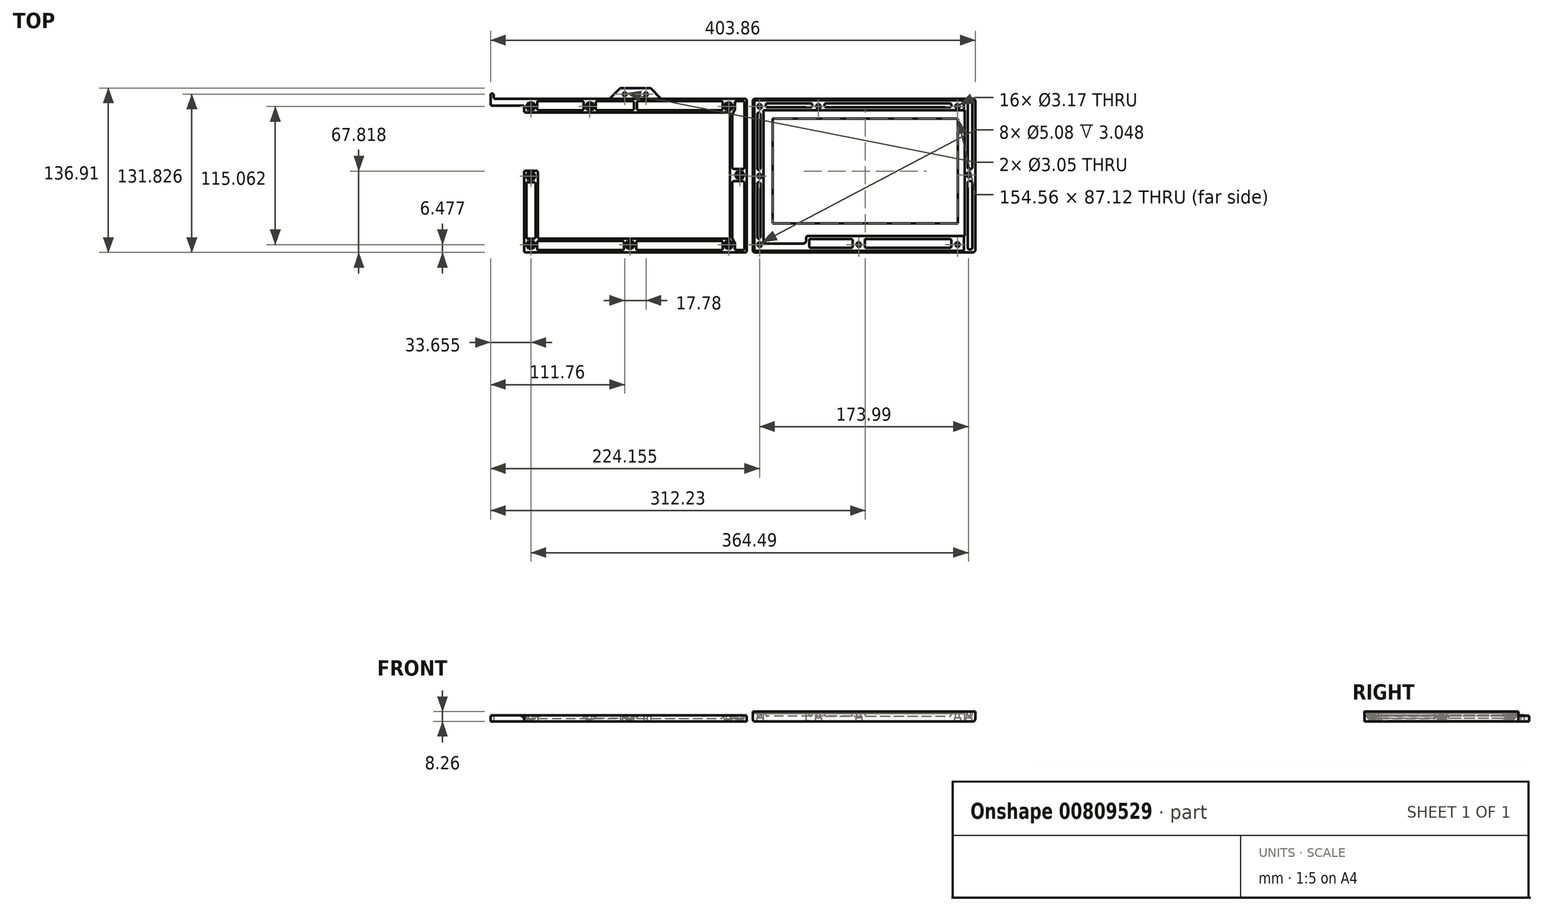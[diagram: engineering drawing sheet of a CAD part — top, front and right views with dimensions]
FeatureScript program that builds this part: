
annotation { "Feature Type Name" : "Feature", "Feature Type Description" : "" }
export const myFeature = defineFeature(function(context is Context, id is Id, definition is map)
    precondition{}
    {
        {
            var Q0;
            Q0=qCreatedBy(makeId("Top.planeOp"),FACE);
            var sketch = newSketch(context, id + "F0", { "sketchPlane" : qUnion([Q0])});
            skLineSegment(sketch, "E0.bottom", {"start": v(2.54, 2.54) * mm, "end": v(187.96, 2.54) * mm});
            skLineSegment(sketch, "E0.top", {"start": v(2.54, 130.56) * mm, "end": v(187.96, 130.56) * mm});
            skLineSegment(sketch, "E0.left", {"start": v(2.54, 2.54) * mm, "end": v(2.54, 130.56) * mm});
            skLineSegment(sketch, "E0.right", {"start": v(187.96, 2.54) * mm, "end": v(187.96, 130.56) * mm});
            skSolve(sketch);
        }
        {
            var Q0;
            Q0 = qSketchRegion(id + "F0", true);
            extrude(context, id + "F1", {"entities" : qUnion([Q0]), "depth" : 8.25 * mm, "offsetDistance" : 25.4 * mm});
        }
        {
            var Q0;
            Q0=makeQuery(id+"F1.opExtrude","CAP_FACE",FACE,{"disambiguationData":[OSD([sQuery(id+"F0.wireOp",EDGE,"E0.bottom"),sQuery(id+"F0.wireOp",EDGE,"E0.top"),sQuery(id+"F0.wireOp",EDGE,"E0.left"),sQuery(id+"F0.wireOp",EDGE,"E0.right")])],"isStart":false});
            var sketch = newSketch(context, id + "F2", { "sketchPlane" : qUnion([Q0])});
            skLineSegment(sketch, "E1.bottom", {"start": v(3.8, 129.29) * mm, "end": v(178.44, 129.29) * mm});
            skLineSegment(sketch, "E1.top", {"start": v(3.81, 3.81) * mm, "end": v(178.44, 3.81) * mm});
            skLineSegment(sketch, "E1.left", {"start": v(3.8, 129.29) * mm, "end": v(3.81, 3.81) * mm});
            skLineSegment(sketch, "E1.right", {"start": v(178.44, 129.29) * mm, "end": v(178.44, 3.81) * mm});
            skSolve(sketch);
        }
        {
            var Q0;
            Q0 = qSketchRegion(id + "F2", true);
            extrude(context, id + "F3", {"entities" : qUnion([Q0]), "operationType" : NewBodyOperationType.REMOVE, "oppositeDirection" : true, "depth" : 1.57 * mm, "offsetDistance" : 25.4 * mm});
        }
        {
            var Q0;
            Q0=makeQuery(id+"F1.opExtrude","CAP_FACE",FACE,{"disambiguationData":[OSD([sQuery(id+"F0.wireOp",EDGE,"E0.bottom"),sQuery(id+"F0.wireOp",EDGE,"E0.top"),sQuery(id+"F0.wireOp",EDGE,"E0.left"),sQuery(id+"F0.wireOp",EDGE,"E0.right")])],"isStart":false});
            var sketch = newSketch(context, id + "F4", { "sketchPlane" : qUnion([Q0])});
            skLineSegment(sketch, "E2.bottom", {"start": v(11.43, 121.03) * mm, "end": v(179.07, 121.03) * mm});
            skLineSegment(sketch, "E2.top", {"start": v(47, 16.38) * mm, "end": v(179.07, 16.38) * mm});
            skLineSegment(sketch, "E2.left", {"start": v(11.43, 121.03) * mm, "end": v(11.43, 10.03) * mm});
            skLineSegment(sketch, "E2.right", {"start": v(179.07, 121.03) * mm, "end": v(179.07, 16.38) * mm});
            skLineSegment(sketch, "E3.top", {"start": v(11.43, 10.03) * mm, "end": v(47, 10.03) * mm});
            skLineSegment(sketch, "E3.right", {"start": v(47, 16.38) * mm, "end": v(47, 10.03) * mm});
            skSolve(sketch);
        }
        {
            var Q0;
            Q0 = qSketchRegion(id + "F4", true);
            extrude(context, id + "F5", {"entities" : qUnion([Q0]), "operationType" : NewBodyOperationType.REMOVE, "oppositeDirection" : true, "depth" : 7.62 * mm, "offsetDistance" : 25.4 * mm});
        }
        {
            var Q0;
            Q0=makeQuery(id+"F5.boolean.opBoolean","COPY",FACE,{"derivedFrom":makeQuery(id+"F5.opExtrude","CAP_FACE",FACE,{"disambiguationData":[OSD([sQuery(id+"F4.wireOp",EDGE,"E2.bottom"),sQuery(id+"F4.wireOp",EDGE,"E2.top"),sQuery(id+"F4.wireOp",EDGE,"E2.left"),sQuery(id+"F4.wireOp",EDGE,"E2.right")])],"isStart":false})});
            var sketch = newSketch(context, id + "F6", { "sketchPlane" : qUnion([Q0])});
            skLineSegment(sketch, "E4.bottom", {"start": v(19.05, 113.92) * mm, "end": v(173.6, 113.92) * mm});
            skLineSegment(sketch, "E4.top", {"start": v(19.05, 26.8) * mm, "end": v(173.6, 26.8) * mm});
            skLineSegment(sketch, "E4.left", {"start": v(19.05, 113.92) * mm, "end": v(19.05, 26.8) * mm});
            skLineSegment(sketch, "E4.right", {"start": v(173.6, 113.92) * mm, "end": v(173.6, 26.8) * mm});
            skSolve(sketch);
        }
        {
            var Q0;
            Q0 = qSketchRegion(id + "F6", true);
            extrude(context, id + "F7", {"entities" : qUnion([Q0]), "operationType" : NewBodyOperationType.REMOVE, "endBound" : BoundingType.UP_TO_NEXT, "oppositeDirection" : true, "depth" : 25.4 * mm, "offsetDistance" : 25.4 * mm});
        }
        {
            var Q0;
            Q0=makeQuery(id+"F1.opExtrude","CAP_FACE",FACE,{"disambiguationData":[OSD([sQuery(id+"F0.wireOp",EDGE,"E0.bottom"),sQuery(id+"F0.wireOp",EDGE,"E0.top"),sQuery(id+"F0.wireOp",EDGE,"E0.left"),sQuery(id+"F0.wireOp",EDGE,"E0.right")])],"isStart":false});
            var sketch = newSketch(context, id + "F8", { "sketchPlane" : qUnion([Q0])});
            skCircle(sketch, "E5", {"center": v(8.25, 124.08) * mm, "radius": 1.59 * mm});
            skCircle(sketch, "E6", {"center": v(57.28, 124.08) * mm, "radius": 1.59 * mm});
            skCircle(sketch, "E7", {"center": v(173.1, 124.08) * mm, "radius": 1.59 * mm});
            skCircle(sketch, "E8", {"center": v(173.1, 9.02) * mm, "radius": 1.59 * mm});
            skCircle(sketch, "E9", {"center": v(8.25, 9.02) * mm, "radius": 1.59 * mm});
            skCircle(sketch, "E10", {"center": v(8.25, 66.17) * mm, "radius": 1.59 * mm});
            skCircle(sketch, "E11", {"center": v(90.8, 9.02) * mm, "radius": 1.59 * mm});
            skCircle(sketch, "E12", {"center": v(182.25, 67) * mm, "radius": 1.59 * mm});
            skSolve(sketch);
        }
        {
            var Q0;
            Q0 = qSketchRegion(id + "F8", true);
            extrude(context, id + "F9", {"entities" : qUnion([Q0]), "operationType" : NewBodyOperationType.REMOVE, "endBound" : BoundingType.THROUGH_ALL, "oppositeDirection" : true, "depth" : 25.4 * mm, "offsetDistance" : 25.4 * mm});
        }
        {
            var Q0;
            Q0=makeQuery(id+"F1.opExtrude","CAP_FACE",FACE,{"disambiguationData":[OSD([sQuery(id+"F0.wireOp",EDGE,"E0.bottom"),sQuery(id+"F0.wireOp",EDGE,"E0.top"),sQuery(id+"F0.wireOp",EDGE,"E0.left"),sQuery(id+"F0.wireOp",EDGE,"E0.right")])],"isStart":true});
            var sketch = newSketch(context, id + "F10", { "sketchPlane" : qUnion([Q0])});
            skCircle(sketch, "E13", {"center": v(173.1, -124.08) * mm, "radius": 2.54 * mm});
            skCircle(sketch, "E14", {"center": v(182.25, -67) * mm, "radius": 2.54 * mm});
            skCircle(sketch, "E15", {"center": v(173.1, -9.02) * mm, "radius": 2.54 * mm});
            skCircle(sketch, "E16", {"center": v(90.8, -9.02) * mm, "radius": 2.54 * mm});
            skCircle(sketch, "E17", {"center": v(8.25, -9.02) * mm, "radius": 2.54 * mm});
            skCircle(sketch, "E18", {"center": v(8.25, -66.17) * mm, "radius": 2.54 * mm});
            skCircle(sketch, "E19", {"center": v(8.25, -124.08) * mm, "radius": 2.54 * mm});
            skCircle(sketch, "E20", {"center": v(57.28, -124.08) * mm, "radius": 2.54 * mm});
            skSolve(sketch);
        }
        {
            var Q0;
            Q0 = qSketchRegion(id + "F10", true);
            extrude(context, id + "F11", {"entities" : qUnion([Q0]), "operationType" : NewBodyOperationType.REMOVE, "oppositeDirection" : true, "depth" : 3.05 * mm, "offsetDistance" : 25.4 * mm});
        }
        {
            var Q0;
            Q0=makeQuery(id+"F1.opExtrude","CAP_EDGE",EDGE,{"disambiguationData":[OSD([sQuery(id+"F0.wireOp",EDGE,"E0.right")])],"isStart":true});
            var Q1;
            Q1=makeQuery(id+"F1.opExtrude","CAP_EDGE",EDGE,{"disambiguationData":[OSD([sQuery(id+"F0.wireOp",EDGE,"E0.bottom")])],"isStart":true});
            var Q2;
            Q2=makeQuery(id+"F1.opExtrude","CAP_EDGE",EDGE,{"disambiguationData":[OSD([sQuery(id+"F0.wireOp",EDGE,"E0.top")])],"isStart":true});
            var Q3;
            Q3=makeQuery(id+"F1.opExtrude","CAP_EDGE",EDGE,{"disambiguationData":[OSD([sQuery(id+"F0.wireOp",EDGE,"E0.left")])],"isStart":true});
            var Q4;
            Q4=makeQuery(id+"F1.opExtrude","SWEPT_EDGE",EDGE,{"disambiguationData":[OSD([sQuery(id+"F0.wireOp",EDGE,"E0.bottom"),sQuery(id+"F0.wireOp",EDGE,"E0.left")])]});
            var Q5;
            Q5=makeQuery(id+"F1.opExtrude","SWEPT_EDGE",EDGE,{"disambiguationData":[OSD([sQuery(id+"F0.wireOp",EDGE,"E0.top"),sQuery(id+"F0.wireOp",EDGE,"E0.left")])]});
            var Q6;
            Q6=makeQuery(id+"F1.opExtrude","SWEPT_EDGE",EDGE,{"disambiguationData":[OSD([sQuery(id+"F0.wireOp",EDGE,"E0.bottom"),sQuery(id+"F0.wireOp",EDGE,"E0.right")])]});
            var Q7;
            Q7=makeQuery(id+"F1.opExtrude","SWEPT_EDGE",EDGE,{"disambiguationData":[OSD([sQuery(id+"F0.wireOp",EDGE,"E0.top"),sQuery(id+"F0.wireOp",EDGE,"E0.right")])]});
            var Q8;
            Q8=makeQuery(id+"F5.boolean.opBoolean","COPY",EDGE,{"derivedFrom":makeQuery(id+"F5.opExtrude","SWEPT_EDGE",EDGE,{"disambiguationData":[OSD([sQuery(id+"F4.wireOp",EDGE,"E2.left"),sQuery(id+"F4.wireOp",EDGE,"E3.top")])]})});
            var Q9;
            Q9=makeQuery(id+"F5.boolean.opBoolean","COPY",EDGE,{"derivedFrom":makeQuery(id+"F5.opExtrude","SWEPT_EDGE",EDGE,{"disambiguationData":[OSD([sQuery(id+"F4.wireOp",EDGE,"E3.top"),sQuery(id+"F4.wireOp",EDGE,"E3.right")])]})});
            var Q10;
            Q10=makeQuery(id+"F5.boolean.opBoolean","COPY",EDGE,{"derivedFrom":makeQuery(id+"F5.opExtrude","SWEPT_EDGE",EDGE,{"disambiguationData":[OSD([sQuery(id+"F4.wireOp",EDGE,"E2.top"),sQuery(id+"F4.wireOp",EDGE,"E3.right")])]})});
            fillet(context, id + "F12", {"entities" : qUnion([Q0, Q1, Q2, Q3, Q4, Q5, Q6, Q7, Q8, Q9, Q10]), "radius" : 1.9 * mm, "tangentPropagation" : true, "allowEdgeOverflow" : false});
        }
        {
            var Q0;
            Q0=makeQuery(id+"F3.boolean.opBoolean","COPY",EDGE,{"derivedFrom":makeQuery(id+"F3.opExtrude","SWEPT_EDGE",EDGE,{"disambiguationData":[OSD([sQuery(id+"F2.wireOp",EDGE,"E1.bottom"),sQuery(id+"F2.wireOp",EDGE,"E1.left")])]})});
            var Q1;
            Q1=makeQuery(id+"F3.boolean.opBoolean","COPY",EDGE,{"derivedFrom":makeQuery(id+"F3.opExtrude","SWEPT_EDGE",EDGE,{"disambiguationData":[OSD([sQuery(id+"F2.wireOp",EDGE,"E1.top"),sQuery(id+"F2.wireOp",EDGE,"E1.left")])]})});
            var Q2;
            Q2=makeQuery(id+"F3.boolean.opBoolean","COPY",EDGE,{"derivedFrom":makeQuery(id+"F3.opExtrude","SWEPT_EDGE",EDGE,{"disambiguationData":[OSD([sQuery(id+"F2.wireOp",EDGE,"E1.top"),sQuery(id+"F2.wireOp",EDGE,"E1.right")])]})});
            var Q3;
            Q3=makeQuery(id+"F3.boolean.opBoolean","COPY",EDGE,{"derivedFrom":makeQuery(id+"F3.opExtrude","SWEPT_EDGE",EDGE,{"disambiguationData":[OSD([sQuery(id+"F2.wireOp",EDGE,"E1.bottom"),sQuery(id+"F2.wireOp",EDGE,"E1.right")])]})});
            fillet(context, id + "F13", {"entities" : qUnion([Q0, Q1, Q2, Q3]), "radius" : 1.27 * mm, "tangentPropagation" : true, "allowEdgeOverflow" : false});
        }
        {
            var Q0;
            Q0=makeQuery(id+"F1.opExtrude","CAP_FACE",FACE,{"disambiguationData":[OSD([sQuery(id+"F0.wireOp",EDGE,"E0.bottom"),sQuery(id+"F0.wireOp",EDGE,"E0.top"),sQuery(id+"F0.wireOp",EDGE,"E0.left"),sQuery(id+"F0.wireOp",EDGE,"E0.right")])],"isStart":false});
            var sketch = newSketch(context, id + "F14", { "sketchPlane" : qUnion([Q0])});
            skLineSegment(sketch, "E21.bottom", {"start": v(181.6, 128.02) * mm, "end": v(185.42, 128.02) * mm});
            skLineSegment(sketch, "E21.top", {"start": v(181.6, 72.09) * mm, "end": v(185.42, 72.09) * mm});
            skLineSegment(sketch, "E21.left", {"start": v(181.6, 128.02) * mm, "end": v(181.6, 72.09) * mm});
            skLineSegment(sketch, "E21.right", {"start": v(185.42, 128.02) * mm, "end": v(185.42, 72.09) * mm});
            skLineSegment(sketch, "E22.bottom", {"start": v(181.6, 61.93) * mm, "end": v(185.42, 61.93) * mm});
            skLineSegment(sketch, "E22.top", {"start": v(181.6, 5.08) * mm, "end": v(185.42, 5.08) * mm});
            skLineSegment(sketch, "E22.left", {"start": v(181.6, 61.93) * mm, "end": v(181.6, 5.08) * mm});
            skLineSegment(sketch, "E22.right", {"start": v(185.42, 61.93) * mm, "end": v(185.42, 5.08) * mm});
            skLineSegment(sketch, "E23.bottom", {"start": v(95.88, 13.84) * mm, "end": v(168.02, 13.84) * mm});
            skLineSegment(sketch, "E23.top", {"start": v(95.88, 6.35) * mm, "end": v(168.02, 6.35) * mm});
            skLineSegment(sketch, "E23.left", {"start": v(95.88, 13.84) * mm, "end": v(95.88, 6.35) * mm});
            skLineSegment(sketch, "E23.right", {"start": v(168.02, 13.84) * mm, "end": v(168.02, 6.35) * mm});
            skLineSegment(sketch, "E24.bottom", {"start": v(85.72, 13.84) * mm, "end": v(49.53, 13.84) * mm});
            skLineSegment(sketch, "E24.top", {"start": v(85.72, 6.35) * mm, "end": v(49.53, 6.35) * mm});
            skLineSegment(sketch, "E24.left", {"start": v(85.72, 13.84) * mm, "end": v(85.72, 6.35) * mm});
            skLineSegment(sketch, "E24.right", {"start": v(49.53, 13.84) * mm, "end": v(49.53, 6.35) * mm});
            skLineSegment(sketch, "E25.bottom", {"start": v(62.36, 126.75) * mm, "end": v(168.02, 126.75) * mm});
            skLineSegment(sketch, "E25.top", {"start": v(62.36, 123.57) * mm, "end": v(168.02, 123.57) * mm});
            skLineSegment(sketch, "E25.left", {"start": v(62.36, 126.75) * mm, "end": v(62.36, 123.57) * mm});
            skLineSegment(sketch, "E25.right", {"start": v(168.02, 126.75) * mm, "end": v(168.02, 123.57) * mm});
            skLineSegment(sketch, "E26.bottom", {"start": v(52.2, 126.75) * mm, "end": v(13.33, 126.75) * mm});
            skLineSegment(sketch, "E26.top", {"start": v(52.2, 123.57) * mm, "end": v(13.33, 123.57) * mm});
            skLineSegment(sketch, "E26.left", {"start": v(52.2, 126.75) * mm, "end": v(52.2, 123.57) * mm});
            skLineSegment(sketch, "E26.right", {"start": v(13.33, 126.75) * mm, "end": v(13.33, 123.57) * mm});
            skLineSegment(sketch, "E27.bottom", {"start": v(8.89, 119) * mm, "end": v(6.35, 119) * mm});
            skLineSegment(sketch, "E27.top", {"start": v(8.89, 71.25) * mm, "end": v(6.35, 71.25) * mm});
            skLineSegment(sketch, "E27.left", {"start": v(8.89, 119) * mm, "end": v(8.89, 71.25) * mm});
            skLineSegment(sketch, "E27.right", {"start": v(6.35, 119) * mm, "end": v(6.35, 71.25) * mm});
            skLineSegment(sketch, "E28.bottom", {"start": v(8.89, 61.09) * mm, "end": v(6.35, 61.09) * mm});
            skLineSegment(sketch, "E28.top", {"start": v(8.9, 14.1) * mm, "end": v(6.35, 14.1) * mm});
            skLineSegment(sketch, "E28.left", {"start": v(8.89, 61.09) * mm, "end": v(8.9, 14.1) * mm});
            skLineSegment(sketch, "E28.right", {"start": v(6.35, 61.09) * mm, "end": v(6.35, 14.1) * mm});
            skSolve(sketch);
        }
        {
            var Q0;
            Q0 = qSketchRegion(id + "F14", true);
            extrude(context, id + "F15", {"entities" : qUnion([Q0]), "operationType" : NewBodyOperationType.REMOVE, "oppositeDirection" : true, "depth" : 3.8 * mm, "offsetDistance" : 25.4 * mm});
        }
        {
            var Q0;
            Q0=makeQuery(id+"F15.boolean.opBoolean","COPY",EDGE,{"derivedFrom":makeQuery(id+"F15.opExtrude","SWEPT_EDGE",EDGE,{"disambiguationData":[OSD([sQuery(id+"F14.wireOp",EDGE,"E22.bottom"),sQuery(id+"F14.wireOp",EDGE,"E22.right")])]})});
            var Q1;
            Q1=makeQuery(id+"F15.boolean.opBoolean","COPY",EDGE,{"derivedFrom":makeQuery(id+"F15.opExtrude","SWEPT_EDGE",EDGE,{"disambiguationData":[OSD([sQuery(id+"F14.wireOp",EDGE,"E22.bottom"),sQuery(id+"F14.wireOp",EDGE,"E22.left")])]})});
            var Q2;
            Q2=makeQuery(id+"F15.boolean.opBoolean","COPY",EDGE,{"derivedFrom":makeQuery(id+"F15.opExtrude","CAP_EDGE",EDGE,{"disambiguationData":[OSD([sQuery(id+"F14.wireOp",EDGE,"E22.left")])],"isStart":false})});
            var Q3;
            Q3=makeQuery(id+"F15.boolean.opBoolean","COPY",EDGE,{"derivedFrom":makeQuery(id+"F15.opExtrude","CAP_EDGE",EDGE,{"disambiguationData":[OSD([sQuery(id+"F14.wireOp",EDGE,"E22.bottom")])],"isStart":false})});
            var Q4;
            Q4=makeQuery(id+"F15.boolean.opBoolean","COPY",EDGE,{"derivedFrom":makeQuery(id+"F15.opExtrude","CAP_EDGE",EDGE,{"disambiguationData":[OSD([sQuery(id+"F14.wireOp",EDGE,"E22.right")])],"isStart":false})});
            var Q5;
            Q5=makeQuery(id+"F15.boolean.opBoolean","COPY",EDGE,{"derivedFrom":makeQuery(id+"F15.opExtrude","SWEPT_EDGE",EDGE,{"disambiguationData":[OSD([sQuery(id+"F14.wireOp",EDGE,"E22.top"),sQuery(id+"F14.wireOp",EDGE,"E22.right")])]})});
            var Q6;
            Q6=makeQuery(id+"F15.boolean.opBoolean","COPY",EDGE,{"derivedFrom":makeQuery(id+"F15.opExtrude","CAP_EDGE",EDGE,{"disambiguationData":[OSD([sQuery(id+"F14.wireOp",EDGE,"E22.top")])],"isStart":false})});
            var Q7;
            Q7=makeQuery(id+"F15.boolean.opBoolean","COPY",EDGE,{"derivedFrom":makeQuery(id+"F15.opExtrude","SWEPT_EDGE",EDGE,{"disambiguationData":[OSD([sQuery(id+"F14.wireOp",EDGE,"E22.top"),sQuery(id+"F14.wireOp",EDGE,"E22.left")])]})});
            var Q8;
            Q8=makeQuery(id+"F15.boolean.opBoolean","COPY",EDGE,{"derivedFrom":makeQuery(id+"F15.opExtrude","SWEPT_EDGE",EDGE,{"disambiguationData":[OSD([sQuery(id+"F14.wireOp",EDGE,"E21.top"),sQuery(id+"F14.wireOp",EDGE,"E21.left")])]})});
            var Q9;
            Q9=makeQuery(id+"F15.boolean.opBoolean","COPY",EDGE,{"derivedFrom":makeQuery(id+"F15.opExtrude","CAP_EDGE",EDGE,{"disambiguationData":[OSD([sQuery(id+"F14.wireOp",EDGE,"E21.left")])],"isStart":false})});
            var Q10;
            Q10=makeQuery(id+"F15.boolean.opBoolean","COPY",EDGE,{"derivedFrom":makeQuery(id+"F15.opExtrude","CAP_EDGE",EDGE,{"disambiguationData":[OSD([sQuery(id+"F14.wireOp",EDGE,"E21.right")])],"isStart":false})});
            var Q11;
            Q11=makeQuery(id+"F15.boolean.opBoolean","COPY",EDGE,{"derivedFrom":makeQuery(id+"F15.opExtrude","SWEPT_EDGE",EDGE,{"disambiguationData":[OSD([sQuery(id+"F14.wireOp",EDGE,"E21.top"),sQuery(id+"F14.wireOp",EDGE,"E21.right")])]})});
            var Q12;
            Q12=makeQuery(id+"F15.boolean.opBoolean","COPY",EDGE,{"derivedFrom":makeQuery(id+"F15.opExtrude","CAP_EDGE",EDGE,{"disambiguationData":[OSD([sQuery(id+"F14.wireOp",EDGE,"E21.top")])],"isStart":false})});
            var Q13;
            Q13=makeQuery(id+"F15.boolean.opBoolean","COPY",EDGE,{"derivedFrom":makeQuery(id+"F15.opExtrude","SWEPT_EDGE",EDGE,{"disambiguationData":[OSD([sQuery(id+"F14.wireOp",EDGE,"E21.bottom"),sQuery(id+"F14.wireOp",EDGE,"E21.right")])]})});
            var Q14;
            Q14=makeQuery(id+"F15.boolean.opBoolean","COPY",EDGE,{"derivedFrom":makeQuery(id+"F15.opExtrude","CAP_EDGE",EDGE,{"disambiguationData":[OSD([sQuery(id+"F14.wireOp",EDGE,"E21.bottom")])],"isStart":false})});
            var Q15;
            Q15=makeQuery(id+"F15.boolean.opBoolean","COPY",EDGE,{"derivedFrom":makeQuery(id+"F15.opExtrude","SWEPT_EDGE",EDGE,{"disambiguationData":[OSD([sQuery(id+"F14.wireOp",EDGE,"E21.bottom"),sQuery(id+"F14.wireOp",EDGE,"E21.left")])]})});
            var Q16;
            Q16=makeQuery(id+"F15.boolean.opBoolean","COPY",EDGE,{"derivedFrom":makeQuery(id+"F15.opExtrude","SWEPT_EDGE",EDGE,{"disambiguationData":[OSD([sQuery(id+"F14.wireOp",EDGE,"E25.bottom"),sQuery(id+"F14.wireOp",EDGE,"E25.right")])]})});
            var Q17;
            Q17=makeQuery(id+"F15.boolean.opBoolean","COPY",EDGE,{"derivedFrom":makeQuery(id+"F15.opExtrude","CAP_EDGE",EDGE,{"disambiguationData":[OSD([sQuery(id+"F14.wireOp",EDGE,"E25.right")])],"isStart":false})});
            var Q18;
            Q18=makeQuery(id+"F15.boolean.opBoolean","COPY",EDGE,{"derivedFrom":makeQuery(id+"F15.opExtrude","CAP_EDGE",EDGE,{"disambiguationData":[OSD([sQuery(id+"F14.wireOp",EDGE,"E25.bottom")])],"isStart":false})});
            var Q19;
            Q19=makeQuery(id+"F15.boolean.opBoolean","COPY",EDGE,{"derivedFrom":makeQuery(id+"F15.opExtrude","SWEPT_EDGE",EDGE,{"disambiguationData":[OSD([sQuery(id+"F14.wireOp",EDGE,"E25.top"),sQuery(id+"F14.wireOp",EDGE,"E25.right")])]})});
            var Q20;
            Q20=makeQuery(id+"F15.boolean.opBoolean","COPY",EDGE,{"derivedFrom":makeQuery(id+"F15.opExtrude","CAP_EDGE",EDGE,{"disambiguationData":[OSD([sQuery(id+"F14.wireOp",EDGE,"E25.left")])],"isStart":false})});
            var Q21;
            Q21=makeQuery(id+"F15.boolean.opBoolean","COPY",EDGE,{"derivedFrom":makeQuery(id+"F15.opExtrude","SWEPT_EDGE",EDGE,{"disambiguationData":[OSD([sQuery(id+"F14.wireOp",EDGE,"E25.bottom"),sQuery(id+"F14.wireOp",EDGE,"E25.left")])]})});
            var Q22;
            Q22=makeQuery(id+"F15.boolean.opBoolean","COPY",EDGE,{"derivedFrom":makeQuery(id+"F15.opExtrude","SWEPT_EDGE",EDGE,{"disambiguationData":[OSD([sQuery(id+"F14.wireOp",EDGE,"E25.top"),sQuery(id+"F14.wireOp",EDGE,"E25.left")])]})});
            var Q23;
            Q23=makeQuery(id+"F15.boolean.opBoolean","COPY",EDGE,{"derivedFrom":makeQuery(id+"F15.opExtrude","SWEPT_EDGE",EDGE,{"disambiguationData":[OSD([sQuery(id+"F14.wireOp",EDGE,"E26.top"),sQuery(id+"F14.wireOp",EDGE,"E26.right")])]})});
            var Q24;
            Q24=makeQuery(id+"F15.boolean.opBoolean","COPY",EDGE,{"derivedFrom":makeQuery(id+"F15.opExtrude","CAP_EDGE",EDGE,{"disambiguationData":[OSD([sQuery(id+"F14.wireOp",EDGE,"E26.right")])],"isStart":false})});
            var Q25;
            Q25=makeQuery(id+"F15.boolean.opBoolean","COPY",EDGE,{"derivedFrom":makeQuery(id+"F15.opExtrude","CAP_EDGE",EDGE,{"disambiguationData":[OSD([sQuery(id+"F14.wireOp",EDGE,"E26.top")])],"isStart":false})});
            var Q26;
            Q26=makeQuery(id+"F15.boolean.opBoolean","COPY",EDGE,{"derivedFrom":makeQuery(id+"F15.opExtrude","SWEPT_EDGE",EDGE,{"disambiguationData":[OSD([sQuery(id+"F14.wireOp",EDGE,"E26.bottom"),sQuery(id+"F14.wireOp",EDGE,"E26.right")])]})});
            var Q27;
            Q27=makeQuery(id+"F15.boolean.opBoolean","COPY",EDGE,{"derivedFrom":makeQuery(id+"F15.opExtrude","CAP_EDGE",EDGE,{"disambiguationData":[OSD([sQuery(id+"F14.wireOp",EDGE,"E26.left")])],"isStart":false})});
            var Q28;
            Q28=makeQuery(id+"F15.boolean.opBoolean","COPY",EDGE,{"derivedFrom":makeQuery(id+"F15.opExtrude","SWEPT_EDGE",EDGE,{"disambiguationData":[OSD([sQuery(id+"F14.wireOp",EDGE,"E26.bottom"),sQuery(id+"F14.wireOp",EDGE,"E26.left")])]})});
            var Q29;
            Q29=makeQuery(id+"F15.boolean.opBoolean","COPY",EDGE,{"derivedFrom":makeQuery(id+"F15.opExtrude","CAP_EDGE",EDGE,{"disambiguationData":[OSD([sQuery(id+"F14.wireOp",EDGE,"E26.bottom")])],"isStart":false})});
            var Q30;
            Q30=makeQuery(id+"F15.boolean.opBoolean","COPY",EDGE,{"derivedFrom":makeQuery(id+"F15.opExtrude","SWEPT_EDGE",EDGE,{"disambiguationData":[OSD([sQuery(id+"F14.wireOp",EDGE,"E26.top"),sQuery(id+"F14.wireOp",EDGE,"E26.left")])]})});
            var Q31;
            Q31=makeQuery(id+"F15.boolean.opBoolean","COPY",EDGE,{"derivedFrom":makeQuery(id+"F15.opExtrude","SWEPT_EDGE",EDGE,{"disambiguationData":[OSD([sQuery(id+"F14.wireOp",EDGE,"E27.bottom"),sQuery(id+"F14.wireOp",EDGE,"E27.right")])]})});
            var Q32;
            Q32=makeQuery(id+"F15.boolean.opBoolean","COPY",EDGE,{"derivedFrom":makeQuery(id+"F15.opExtrude","CAP_EDGE",EDGE,{"disambiguationData":[OSD([sQuery(id+"F14.wireOp",EDGE,"E27.bottom")])],"isStart":false})});
            var Q33;
            Q33=makeQuery(id+"F15.boolean.opBoolean","COPY",EDGE,{"derivedFrom":makeQuery(id+"F15.opExtrude","SWEPT_EDGE",EDGE,{"disambiguationData":[OSD([sQuery(id+"F14.wireOp",EDGE,"E27.bottom"),sQuery(id+"F14.wireOp",EDGE,"E27.left")])]})});
            var Q34;
            Q34=makeQuery(id+"F15.boolean.opBoolean","COPY",EDGE,{"derivedFrom":makeQuery(id+"F15.opExtrude","CAP_EDGE",EDGE,{"disambiguationData":[OSD([sQuery(id+"F14.wireOp",EDGE,"E27.left")])],"isStart":false})});
            var Q35;
            Q35=makeQuery(id+"F15.boolean.opBoolean","COPY",EDGE,{"derivedFrom":makeQuery(id+"F15.opExtrude","SWEPT_EDGE",EDGE,{"disambiguationData":[OSD([sQuery(id+"F14.wireOp",EDGE,"E28.bottom"),sQuery(id+"F14.wireOp",EDGE,"E28.left")])]})});
            var Q36;
            Q36=makeQuery(id+"F15.boolean.opBoolean","COPY",EDGE,{"derivedFrom":makeQuery(id+"F15.opExtrude","CAP_EDGE",EDGE,{"disambiguationData":[OSD([sQuery(id+"F14.wireOp",EDGE,"E28.left")])],"isStart":false})});
            var Q37;
            Q37=makeQuery(id+"F15.boolean.opBoolean","COPY",EDGE,{"derivedFrom":makeQuery(id+"F15.opExtrude","CAP_EDGE",EDGE,{"disambiguationData":[OSD([sQuery(id+"F14.wireOp",EDGE,"E28.bottom")])],"isStart":false})});
            var Q38;
            Q38=makeQuery(id+"F15.boolean.opBoolean","COPY",EDGE,{"derivedFrom":makeQuery(id+"F15.opExtrude","SWEPT_EDGE",EDGE,{"disambiguationData":[OSD([sQuery(id+"F14.wireOp",EDGE,"E28.bottom"),sQuery(id+"F14.wireOp",EDGE,"E28.right")])]})});
            var Q39;
            Q39=makeQuery(id+"F15.boolean.opBoolean","COPY",EDGE,{"derivedFrom":makeQuery(id+"F15.opExtrude","CAP_EDGE",EDGE,{"disambiguationData":[OSD([sQuery(id+"F14.wireOp",EDGE,"E27.right")])],"isStart":false})});
            var Q40;
            Q40=makeQuery(id+"F15.boolean.opBoolean","COPY",EDGE,{"derivedFrom":makeQuery(id+"F15.opExtrude","SWEPT_EDGE",EDGE,{"disambiguationData":[OSD([sQuery(id+"F14.wireOp",EDGE,"E27.top"),sQuery(id+"F14.wireOp",EDGE,"E27.right")])]})});
            var Q41;
            Q41=makeQuery(id+"F15.boolean.opBoolean","COPY",EDGE,{"derivedFrom":makeQuery(id+"F15.opExtrude","CAP_EDGE",EDGE,{"disambiguationData":[OSD([sQuery(id+"F14.wireOp",EDGE,"E27.top")])],"isStart":false})});
            var Q42;
            Q42=makeQuery(id+"F15.boolean.opBoolean","COPY",EDGE,{"derivedFrom":makeQuery(id+"F15.opExtrude","SWEPT_EDGE",EDGE,{"disambiguationData":[OSD([sQuery(id+"F14.wireOp",EDGE,"E27.top"),sQuery(id+"F14.wireOp",EDGE,"E27.left")])]})});
            var Q43;
            Q43=makeQuery(id+"F15.boolean.opBoolean","COPY",EDGE,{"derivedFrom":makeQuery(id+"F15.opExtrude","SWEPT_EDGE",EDGE,{"disambiguationData":[OSD([sQuery(id+"F14.wireOp",EDGE,"E28.top"),sQuery(id+"F14.wireOp",EDGE,"E28.left")])]})});
            var Q44;
            Q44=makeQuery(id+"F15.boolean.opBoolean","COPY",EDGE,{"derivedFrom":makeQuery(id+"F15.opExtrude","CAP_EDGE",EDGE,{"disambiguationData":[OSD([sQuery(id+"F14.wireOp",EDGE,"E28.top")])],"isStart":false})});
            var Q45;
            Q45=makeQuery(id+"F15.boolean.opBoolean","COPY",EDGE,{"derivedFrom":makeQuery(id+"F15.opExtrude","SWEPT_EDGE",EDGE,{"disambiguationData":[OSD([sQuery(id+"F14.wireOp",EDGE,"E28.top"),sQuery(id+"F14.wireOp",EDGE,"E28.right")])]})});
            var Q46;
            Q46=makeQuery(id+"F15.boolean.opBoolean","COPY",EDGE,{"derivedFrom":makeQuery(id+"F15.opExtrude","CAP_EDGE",EDGE,{"disambiguationData":[OSD([sQuery(id+"F14.wireOp",EDGE,"E28.right")])],"isStart":false})});
            var Q47;
            Q47=makeQuery(id+"F15.boolean.opBoolean","COPY",EDGE,{"derivedFrom":makeQuery(id+"F15.opExtrude","SWEPT_EDGE",EDGE,{"disambiguationData":[OSD([sQuery(id+"F14.wireOp",EDGE,"E24.top"),sQuery(id+"F14.wireOp",EDGE,"E24.right")])]})});
            var Q48;
            Q48=makeQuery(id+"F15.boolean.opBoolean","COPY",EDGE,{"derivedFrom":makeQuery(id+"F15.opExtrude","CAP_EDGE",EDGE,{"disambiguationData":[OSD([sQuery(id+"F14.wireOp",EDGE,"E24.right")])],"isStart":false})});
            var Q49;
            Q49=makeQuery(id+"F15.boolean.opBoolean","COPY",EDGE,{"derivedFrom":makeQuery(id+"F15.opExtrude","CAP_EDGE",EDGE,{"disambiguationData":[OSD([sQuery(id+"F14.wireOp",EDGE,"E24.top")])],"isStart":false})});
            var Q50;
            Q50=makeQuery(id+"F15.boolean.opBoolean","COPY",EDGE,{"derivedFrom":makeQuery(id+"F15.opExtrude","SWEPT_EDGE",EDGE,{"disambiguationData":[OSD([sQuery(id+"F14.wireOp",EDGE,"E24.bottom"),sQuery(id+"F14.wireOp",EDGE,"E24.right")])]})});
            var Q51;
            Q51=makeQuery(id+"F15.boolean.opBoolean","COPY",EDGE,{"derivedFrom":makeQuery(id+"F15.opExtrude","CAP_EDGE",EDGE,{"disambiguationData":[OSD([sQuery(id+"F14.wireOp",EDGE,"E24.bottom")])],"isStart":false})});
            var Q52;
            Q52=makeQuery(id+"F15.boolean.opBoolean","COPY",FACE,{"derivedFrom":makeQuery(id+"F15.opExtrude","CAP_FACE",FACE,{"disambiguationData":[OSD([sQuery(id+"F14.wireOp",EDGE,"E23.bottom"),sQuery(id+"F14.wireOp",EDGE,"E23.top"),sQuery(id+"F14.wireOp",EDGE,"E23.left"),sQuery(id+"F14.wireOp",EDGE,"E23.right")])],"isStart":false})});
            var Q53;
            Q53=makeQuery(id+"F15.boolean.opBoolean","COPY",EDGE,{"derivedFrom":makeQuery(id+"F15.opExtrude","SWEPT_EDGE",EDGE,{"disambiguationData":[OSD([sQuery(id+"F14.wireOp",EDGE,"E23.top"),sQuery(id+"F14.wireOp",EDGE,"E23.left")])]})});
            var Q54;
            Q54=makeQuery(id+"F15.boolean.opBoolean","COPY",EDGE,{"derivedFrom":makeQuery(id+"F15.opExtrude","CAP_EDGE",EDGE,{"disambiguationData":[OSD([sQuery(id+"F14.wireOp",EDGE,"E24.left")])],"isStart":false})});
            var Q55;
            Q55=makeQuery(id+"F15.boolean.opBoolean","COPY",EDGE,{"derivedFrom":makeQuery(id+"F15.opExtrude","SWEPT_EDGE",EDGE,{"disambiguationData":[OSD([sQuery(id+"F14.wireOp",EDGE,"E24.top"),sQuery(id+"F14.wireOp",EDGE,"E24.left")])]})});
            var Q56;
            Q56=makeQuery(id+"F15.boolean.opBoolean","COPY",EDGE,{"derivedFrom":makeQuery(id+"F15.opExtrude","SWEPT_EDGE",EDGE,{"disambiguationData":[OSD([sQuery(id+"F14.wireOp",EDGE,"E24.bottom"),sQuery(id+"F14.wireOp",EDGE,"E24.left")])]})});
            var Q57;
            Q57=makeQuery(id+"F15.boolean.opBoolean","COPY",EDGE,{"derivedFrom":makeQuery(id+"F15.opExtrude","SWEPT_EDGE",EDGE,{"disambiguationData":[OSD([sQuery(id+"F14.wireOp",EDGE,"E23.bottom"),sQuery(id+"F14.wireOp",EDGE,"E23.left")])]})});
            var Q58;
            Q58=makeQuery(id+"F15.boolean.opBoolean","COPY",EDGE,{"derivedFrom":makeQuery(id+"F15.opExtrude","SWEPT_EDGE",EDGE,{"disambiguationData":[OSD([sQuery(id+"F14.wireOp",EDGE,"E23.top"),sQuery(id+"F14.wireOp",EDGE,"E23.right")])]})});
            var Q59;
            Q59=makeQuery(id+"F15.boolean.opBoolean","COPY",EDGE,{"derivedFrom":makeQuery(id+"F15.opExtrude","SWEPT_EDGE",EDGE,{"disambiguationData":[OSD([sQuery(id+"F14.wireOp",EDGE,"E23.bottom"),sQuery(id+"F14.wireOp",EDGE,"E23.right")])]})});
            fillet(context, id + "F16", {"entities" : qUnion([Q0, Q1, Q2, Q3, Q4, Q5, Q6, Q7, Q8, Q9, Q10, Q11, Q12, Q13, Q14, Q15, Q16, Q17, Q18, Q19, Q20, Q21, Q22, Q23, Q24, Q25, Q26, Q27, Q28, Q29, Q30, Q31, Q32, Q33, Q34, Q35, Q36, Q37, Q38, Q39, Q40, Q41, Q42, Q43, Q44, Q45, Q46, Q47, Q48, Q49, Q50, Q51, Q52, Q53, Q54, Q55, Q56, Q57, Q58, Q59]), "radius" : 1.27 * mm, "tangentPropagation" : true, "allowEdgeOverflow" : false});
        }
        {
            var Q0;
            Q0=qCreatedBy(makeId("Top.planeOp"),FACE);
            var sketch = newSketch(context, id + "F17", { "sketchPlane" : qUnion([Q0])});
            skLineSegment(sketch, "E29.bottom", {"start": v(-187.96, 2.54) * mm, "end": v(-2.54, 2.54) * mm});
            skLineSegment(sketch, "E29.top", {"start": v(-187.96, 130.56) * mm, "end": v(-2.54, 130.56) * mm});
            skLineSegment(sketch, "E29.left", {"start": v(-187.96, 2.54) * mm, "end": v(-187.96, 70.61) * mm});
            skLineSegment(sketch, "E29.right", {"start": v(-2.54, 2.54) * mm, "end": v(-2.54, 130.56) * mm});
            skLineSegment(sketch, "E30.bottom", {"start": v(-187.96, 119.13) * mm, "end": v(-16.26, 119.13) * mm});
            skLineSegment(sketch, "E30.top", {"start": v(-176.53, 13.97) * mm, "end": v(-16.26, 13.97) * mm});
            skLineSegment(sketch, "E30.left", {"start": v(-176.53, 70.61) * mm, "end": v(-176.53, 13.97) * mm});
            skLineSegment(sketch, "E30.right", {"start": v(-16.26, 119.13) * mm, "end": v(-16.26, 13.97) * mm});
            skLineSegment(sketch, "E31", {"start": v(-176.53, 70.61) * mm, "end": v(-187.96, 70.61) * mm});
            skLineSegment(sketch, "E32.trimOffspring", {"start": v(-187.96, 119.13) * mm, "end": v(-187.96, 124.84) * mm});
            skCircle(sketch, "E33", {"center": v(-182.25, 124.08) * mm, "radius": 1.59 * mm});
            skCircle(sketch, "E34", {"center": v(-133.22, 124.08) * mm, "radius": 1.59 * mm});
            skCircle(sketch, "E35", {"center": v(-17.4, 124.08) * mm, "radius": 1.59 * mm});
            skCircle(sketch, "E36", {"center": v(-17.4, 9.02) * mm, "radius": 1.59 * mm});
            skCircle(sketch, "E37", {"center": v(-182.25, 9.02) * mm, "radius": 1.59 * mm});
            skCircle(sketch, "E38", {"center": v(-182.25, 66.17) * mm, "radius": 1.59 * mm});
            skCircle(sketch, "E39", {"center": v(-99.7, 9.02) * mm, "radius": 1.59 * mm});
            skCircle(sketch, "E40", {"center": v(-8.26, 67) * mm, "radius": 1.59 * mm});
            skLineSegment(sketch, "E41", {"start": v(-116.84, 130.56) * mm, "end": v(-107.95, 139.45) * mm});
            skLineSegment(sketch, "E42", {"start": v(-107.95, 139.45) * mm, "end": v(-82.55, 139.45) * mm});
            skLineSegment(sketch, "E43", {"start": v(-82.55, 139.45) * mm, "end": v(-73.66, 130.56) * mm});
            skLineSegment(sketch, "E44", {"start": v(-187.96, 130.56) * mm, "end": v(-213.36, 130.56) * mm});
            skLineSegment(sketch, "E45", {"start": v(-213.36, 130.56) * mm, "end": v(-213.36, 135) * mm});
            skLineSegment(sketch, "E46", {"start": v(-213.36, 135) * mm, "end": v(-215.9, 135) * mm});
            skLineSegment(sketch, "E47", {"start": v(-215.9, 135) * mm, "end": v(-215.9, 124.84) * mm});
            skLineSegment(sketch, "E48", {"start": v(-215.9, 124.84) * mm, "end": v(-187.96, 124.84) * mm});
            skSolve(sketch);
        }
        {
            var Q0;
            Q0 = qSketchRegion(id + "F17", true);
            extrude(context, id + "F18", {"entities" : qUnion([Q0]), "depth" : 5.08 * mm, "offsetDistance" : 25.4 * mm});
        }
        {
            var Q0;
            Q0=makeQuery(id+"F18.opExtrude","CAP_FACE",FACE,{"disambiguationData":[OSD([sQuery(id+"F17.wireOp",EDGE,"E29.bottom"),sQuery(id+"F17.wireOp",EDGE,"E29.top"),sQuery(id+"F17.wireOp",EDGE,"E29.left"),sQuery(id+"F17.wireOp",EDGE,"E29.right"),sQuery(id+"F17.wireOp",EDGE,"E30.bottom"),sQuery(id+"F17.wireOp",EDGE,"E30.top"),sQuery(id+"F17.wireOp",EDGE,"E30.left"),sQuery(id+"F17.wireOp",EDGE,"E30.right"),sQuery(id+"F17.wireOp",EDGE,"E31"),sQuery(id+"F17.wireOp",EDGE,"E32.trimOffspring"),sQuery(id+"F17.wireOp",EDGE,"E33"),sQuery(id+"F17.wireOp",EDGE,"E34"),sQuery(id+"F17.wireOp",EDGE,"E35"),sQuery(id+"F17.wireOp",EDGE,"E36"),sQuery(id+"F17.wireOp",EDGE,"E37"),sQuery(id+"F17.wireOp",EDGE,"E38"),sQuery(id+"F17.wireOp",EDGE,"E39"),sQuery(id+"F17.wireOp",EDGE,"E40")])],"isStart":false});
            var sketch = newSketch(context, id + "F19", { "sketchPlane" : qUnion([Q0])});
            skCircle(sketch, "E49.cCircle", {"center": v(-182.25, 124.08) * mm, "radius": 3.18 * mm, "construction": true});
            skLineSegment(sketch, "E49.0", {"start": v(-178.58, 124.08) * mm, "end": v(-180.41, 120.9) * mm});
            skLineSegment(sketch, "E49.1", {"start": v(-180.41, 120.9) * mm, "end": v(-184.08, 120.9) * mm});
            skLineSegment(sketch, "E49.2", {"start": v(-184.08, 120.9) * mm, "end": v(-185.91, 124.08) * mm});
            skLineSegment(sketch, "E49.3", {"start": v(-185.91, 124.08) * mm, "end": v(-184.08, 127.25) * mm});
            skLineSegment(sketch, "E49.4", {"start": v(-184.08, 127.25) * mm, "end": v(-180.41, 127.25) * mm});
            skLineSegment(sketch, "E49.5", {"start": v(-180.41, 127.25) * mm, "end": v(-178.58, 124.08) * mm});
            skPoint(sketch, "E49.0.midPoint", {"position": v(-179.5, 122.5) * mm});
            skCircle(sketch, "E50.cCircle", {"center": v(-133.22, 124.08) * mm, "radius": 3.18 * mm, "construction": true});
            skLineSegment(sketch, "E50.0", {"start": v(-129.56, 124.08) * mm, "end": v(-131.39, 120.9) * mm});
            skLineSegment(sketch, "E50.1", {"start": v(-131.39, 120.9) * mm, "end": v(-135.06, 120.9) * mm});
            skLineSegment(sketch, "E50.2", {"start": v(-135.06, 120.9) * mm, "end": v(-136.89, 124.08) * mm});
            skLineSegment(sketch, "E50.3", {"start": v(-136.89, 124.08) * mm, "end": v(-135.06, 127.25) * mm});
            skLineSegment(sketch, "E50.4", {"start": v(-135.06, 127.25) * mm, "end": v(-131.39, 127.25) * mm});
            skLineSegment(sketch, "E50.5", {"start": v(-131.39, 127.25) * mm, "end": v(-129.56, 124.08) * mm});
            skPoint(sketch, "E50.0.midPoint", {"position": v(-130.47, 122.5) * mm});
            skCircle(sketch, "E51.cCircle", {"center": v(-17.4, 124.08) * mm, "radius": 3.18 * mm, "construction": true});
            skLineSegment(sketch, "E51.0", {"start": v(-13.73, 124.08) * mm, "end": v(-15.57, 120.9) * mm});
            skLineSegment(sketch, "E51.1", {"start": v(-15.57, 120.9) * mm, "end": v(-19.23, 120.9) * mm});
            skLineSegment(sketch, "E51.2", {"start": v(-19.23, 120.9) * mm, "end": v(-21.07, 124.08) * mm});
            skLineSegment(sketch, "E51.3", {"start": v(-21.07, 124.08) * mm, "end": v(-19.23, 127.25) * mm});
            skLineSegment(sketch, "E51.4", {"start": v(-19.23, 127.25) * mm, "end": v(-15.57, 127.25) * mm});
            skLineSegment(sketch, "E51.5", {"start": v(-15.57, 127.25) * mm, "end": v(-13.73, 124.08) * mm});
            skPoint(sketch, "E51.0.midPoint", {"position": v(-14.65, 122.5) * mm});
            skCircle(sketch, "E52.cCircle", {"center": v(-8.26, 67) * mm, "radius": 3.18 * mm, "construction": true});
            skLineSegment(sketch, "E52.0", {"start": v(-4.59, 67) * mm, "end": v(-6.42, 63.83) * mm});
            skLineSegment(sketch, "E52.1", {"start": v(-6.42, 63.83) * mm, "end": v(-10.09, 63.83) * mm});
            skLineSegment(sketch, "E52.2", {"start": v(-10.09, 63.83) * mm, "end": v(-11.92, 67) * mm});
            skLineSegment(sketch, "E52.3", {"start": v(-11.92, 67) * mm, "end": v(-10.09, 70.18) * mm});
            skLineSegment(sketch, "E52.4", {"start": v(-10.09, 70.18) * mm, "end": v(-6.42, 70.18) * mm});
            skLineSegment(sketch, "E52.5", {"start": v(-6.42, 70.18) * mm, "end": v(-4.59, 67) * mm});
            skPoint(sketch, "E52.0.midPoint", {"position": v(-5.5, 65.42) * mm});
            skCircle(sketch, "E53.cCircle", {"center": v(-17.4, 9.02) * mm, "radius": 3.18 * mm, "construction": true});
            skLineSegment(sketch, "E53.0", {"start": v(-13.73, 9.02) * mm, "end": v(-15.57, 5.84) * mm});
            skLineSegment(sketch, "E53.1", {"start": v(-15.57, 5.84) * mm, "end": v(-19.23, 5.84) * mm});
            skLineSegment(sketch, "E53.2", {"start": v(-19.23, 5.84) * mm, "end": v(-21.07, 9.02) * mm});
            skLineSegment(sketch, "E53.3", {"start": v(-21.07, 9.02) * mm, "end": v(-19.23, 12.2) * mm});
            skLineSegment(sketch, "E53.4", {"start": v(-19.23, 12.2) * mm, "end": v(-15.57, 12.2) * mm});
            skLineSegment(sketch, "E53.5", {"start": v(-15.57, 12.2) * mm, "end": v(-13.73, 9.02) * mm});
            skPoint(sketch, "E53.0.midPoint", {"position": v(-14.65, 7.43) * mm});
            skCircle(sketch, "E54.cCircle", {"center": v(-99.7, 9.02) * mm, "radius": 3.18 * mm, "construction": true});
            skLineSegment(sketch, "E54.0", {"start": v(-96.03, 9.02) * mm, "end": v(-97.86, 5.84) * mm});
            skLineSegment(sketch, "E54.1", {"start": v(-97.86, 5.84) * mm, "end": v(-101.53, 5.84) * mm});
            skLineSegment(sketch, "E54.2", {"start": v(-101.53, 5.84) * mm, "end": v(-103.36, 9.02) * mm});
            skLineSegment(sketch, "E54.3", {"start": v(-103.36, 9.02) * mm, "end": v(-101.53, 12.2) * mm});
            skLineSegment(sketch, "E54.4", {"start": v(-101.53, 12.2) * mm, "end": v(-97.86, 12.2) * mm});
            skLineSegment(sketch, "E54.5", {"start": v(-97.86, 12.2) * mm, "end": v(-96.03, 9.02) * mm});
            skPoint(sketch, "E54.0.midPoint", {"position": v(-96.95, 7.43) * mm});
            skCircle(sketch, "E55.cCircle", {"center": v(-182.25, 9.02) * mm, "radius": 3.18 * mm, "construction": true});
            skLineSegment(sketch, "E55.0", {"start": v(-178.58, 9.02) * mm, "end": v(-180.41, 5.84) * mm});
            skLineSegment(sketch, "E55.1", {"start": v(-180.41, 5.84) * mm, "end": v(-184.08, 5.84) * mm});
            skLineSegment(sketch, "E55.2", {"start": v(-184.08, 5.84) * mm, "end": v(-185.91, 9.02) * mm});
            skLineSegment(sketch, "E55.3", {"start": v(-185.91, 9.02) * mm, "end": v(-184.08, 12.2) * mm});
            skLineSegment(sketch, "E55.4", {"start": v(-184.08, 12.2) * mm, "end": v(-180.41, 12.2) * mm});
            skLineSegment(sketch, "E55.5", {"start": v(-180.41, 12.2) * mm, "end": v(-178.58, 9.02) * mm});
            skPoint(sketch, "E55.0.midPoint", {"position": v(-179.5, 7.43) * mm});
            skCircle(sketch, "E56.cCircle", {"center": v(-182.25, 66.17) * mm, "radius": 3.18 * mm, "construction": true});
            skLineSegment(sketch, "E56.0", {"start": v(-178.58, 66.17) * mm, "end": v(-180.41, 63) * mm});
            skLineSegment(sketch, "E56.1", {"start": v(-180.41, 63) * mm, "end": v(-184.08, 63) * mm});
            skLineSegment(sketch, "E56.2", {"start": v(-184.08, 63) * mm, "end": v(-185.91, 66.17) * mm});
            skLineSegment(sketch, "E56.3", {"start": v(-185.91, 66.17) * mm, "end": v(-184.08, 69.34) * mm});
            skLineSegment(sketch, "E56.4", {"start": v(-184.08, 69.34) * mm, "end": v(-180.41, 69.34) * mm});
            skLineSegment(sketch, "E56.5", {"start": v(-180.41, 69.34) * mm, "end": v(-178.58, 66.17) * mm});
            skPoint(sketch, "E56.0.midPoint", {"position": v(-179.5, 64.58) * mm});
            skSolve(sketch);
        }
        {
            var Q0;
            Q0 = qSketchRegion(id + "F19", true);
            extrude(context, id + "F20", {"entities" : qUnion([Q0]), "operationType" : NewBodyOperationType.REMOVE, "oppositeDirection" : true, "depth" : 3.3 * mm, "offsetDistance" : 25.4 * mm});
        }
        {
            var Q0;
            Q0=makeQuery(id+"F18.opExtrude","CAP_FACE",FACE,{"disambiguationData":[OSD([sQuery(id+"F17.wireOp",EDGE,"E29.bottom"),sQuery(id+"F17.wireOp",EDGE,"E29.top"),sQuery(id+"F17.wireOp",EDGE,"E29.left"),sQuery(id+"F17.wireOp",EDGE,"E29.right"),sQuery(id+"F17.wireOp",EDGE,"E30.bottom"),sQuery(id+"F17.wireOp",EDGE,"E30.top"),sQuery(id+"F17.wireOp",EDGE,"E30.left"),sQuery(id+"F17.wireOp",EDGE,"E30.right"),sQuery(id+"F17.wireOp",EDGE,"E31"),sQuery(id+"F17.wireOp",EDGE,"E32.trimOffspring"),sQuery(id+"F17.wireOp",EDGE,"E33"),sQuery(id+"F17.wireOp",EDGE,"E34"),sQuery(id+"F17.wireOp",EDGE,"E35"),sQuery(id+"F17.wireOp",EDGE,"E36"),sQuery(id+"F17.wireOp",EDGE,"E37"),sQuery(id+"F17.wireOp",EDGE,"E38"),sQuery(id+"F17.wireOp",EDGE,"E39"),sQuery(id+"F17.wireOp",EDGE,"E40")])],"isStart":false});
            var sketch = newSketch(context, id + "F21", { "sketchPlane" : qUnion([Q0])});
            skLineSegment(sketch, "E57.left", {"start": v(-177.17, 128.65) * mm, "end": v(-177.17, 121.03) * mm});
            skLineSegment(sketch, "E57.right", {"start": v(-138.3, 128.65) * mm, "end": v(-138.3, 121.03) * mm});
            skLineSegment(sketch, "E58.left", {"start": v(-128.14, 128.65) * mm, "end": v(-128.14, 121.03) * mm});
            skLineSegment(sketch, "E58.right", {"start": v(-22.48, 128.65) * mm, "end": v(-22.48, 121.03) * mm});
            skLineSegment(sketch, "E59.right", {"start": v(-12.32, 128.65) * mm, "end": v(-12.32, 121.45) * mm});
            skLineSegment(sketch, "E60.bottom", {"start": v(-4.44, 61.93) * mm, "end": v(-14.35, 61.93) * mm});
            skLineSegment(sketch, "E61.right", {"start": v(-12.32, 10.45) * mm, "end": v(-12.32, 4.45) * mm});
            skLineSegment(sketch, "E62", {"start": v(-177.17, 121.03) * mm, "end": v(-138.3, 121.03) * mm});
            skLineSegment(sketch, "E63", {"start": v(-4.45, 128.65) * mm, "end": v(-12.32, 128.65) * mm});
            skLineSegment(sketch, "E64.trimOffspring", {"start": v(-128.14, 121.03) * mm, "end": v(-96.52, 121.03) * mm});
            skLineSegment(sketch, "E65.trimOffspring", {"start": v(-138.3, 128.65) * mm, "end": v(-177.17, 128.65) * mm});
            skLineSegment(sketch, "E66.trimOffspring", {"start": v(-22.48, 128.65) * mm, "end": v(-93.98, 128.65) * mm});
            skLineSegment(sketch, "E67", {"start": v(-14.35, 13.97) * mm, "end": v(-14.35, 61.93) * mm});
            skPoint(sketch, "E67.endSnap0", {"position": v(-14.65, 10.6) * mm});
            skLineSegment(sketch, "E68", {"start": v(-4.44, 4.45) * mm, "end": v(-12.32, 4.45) * mm});
            skLineSegment(sketch, "E69.trimOffspring", {"start": v(-4.44, 61.93) * mm, "end": v(-4.44, 4.45) * mm});
            skLineSegment(sketch, "E70.top", {"start": v(-4.44, 72.09) * mm, "end": v(-14.35, 72.09) * mm});
            skLineSegment(sketch, "E70.left", {"start": v(-4.45, 128.65) * mm, "end": v(-4.44, 72.09) * mm});
            skLineSegment(sketch, "E70.right", {"start": v(-14.35, 117.93) * mm, "end": v(-14.35, 72.09) * mm});
            skLineSegment(sketch, "E71", {"start": v(-14.35, 117.93) * mm, "end": v(-12.32, 121.45) * mm});
            skLineSegment(sketch, "E72", {"start": v(-12.32, 10.45) * mm, "end": v(-14.35, 13.97) * mm});
            skLineSegment(sketch, "E73.bottom", {"start": v(-94.62, 12.07) * mm, "end": v(-22.48, 12.07) * mm});
            skLineSegment(sketch, "E73.top", {"start": v(-94.62, 4.45) * mm, "end": v(-22.48, 4.45) * mm});
            skLineSegment(sketch, "E73.left", {"start": v(-94.62, 12.07) * mm, "end": v(-94.62, 4.45) * mm});
            skLineSegment(sketch, "E73.right", {"start": v(-22.48, 12.07) * mm, "end": v(-22.48, 4.45) * mm});
            skLineSegment(sketch, "E74.bottom", {"start": v(-177.17, 12.06) * mm, "end": v(-104.78, 12.07) * mm});
            skLineSegment(sketch, "E74.top", {"start": v(-177.17, 4.44) * mm, "end": v(-104.78, 4.45) * mm});
            skLineSegment(sketch, "E74.left", {"start": v(-177.17, 12.06) * mm, "end": v(-177.17, 4.44) * mm});
            skLineSegment(sketch, "E74.right", {"start": v(-104.78, 12.07) * mm, "end": v(-104.78, 4.45) * mm});
            skLineSegment(sketch, "E75.bottom", {"start": v(-186.05, 61.09) * mm, "end": v(-178.44, 61.09) * mm});
            skLineSegment(sketch, "E75.top", {"start": v(-186.05, 14.1) * mm, "end": v(-178.44, 14.1) * mm});
            skLineSegment(sketch, "E75.left", {"start": v(-186.05, 61.09) * mm, "end": v(-186.05, 14.1) * mm});
            skLineSegment(sketch, "E75.right", {"start": v(-178.44, 61.09) * mm, "end": v(-178.44, 14.1) * mm});
            skLineSegment(sketch, "E76", {"start": v(-96.52, 128.65) * mm, "end": v(-96.52, 121.03) * mm});
            skLineSegment(sketch, "E77", {"start": v(-93.98, 121.03) * mm, "end": v(-93.98, 128.65) * mm});
            skLineSegment(sketch, "E78.trimOffspring", {"start": v(-96.52, 128.65) * mm, "end": v(-128.14, 128.65) * mm});
            skLineSegment(sketch, "E79.trimOffspring", {"start": v(-93.98, 121.03) * mm, "end": v(-22.48, 121.03) * mm});
            skSolve(sketch);
        }
        {
            var Q0;
            Q0 = qSketchRegion(id + "F21", true);
            extrude(context, id + "F22", {"entities" : qUnion([Q0]), "operationType" : NewBodyOperationType.REMOVE, "oppositeDirection" : true, "depth" : 2.54 * mm, "offsetDistance" : 25.4 * mm});
        }
        {
            var Q0;
            Q0=makeQuery(id+"F18.opExtrude","CAP_FACE",FACE,{"disambiguationData":[OSD([sQuery(id+"F17.wireOp",EDGE,"E29.bottom"),sQuery(id+"F17.wireOp",EDGE,"E29.top"),sQuery(id+"F17.wireOp",EDGE,"E29.left"),sQuery(id+"F17.wireOp",EDGE,"E29.right"),sQuery(id+"F17.wireOp",EDGE,"E30.bottom"),sQuery(id+"F17.wireOp",EDGE,"E30.top"),sQuery(id+"F17.wireOp",EDGE,"E30.left"),sQuery(id+"F17.wireOp",EDGE,"E30.right"),sQuery(id+"F17.wireOp",EDGE,"E31"),sQuery(id+"F17.wireOp",EDGE,"E32.trimOffspring"),sQuery(id+"F17.wireOp",EDGE,"E33"),sQuery(id+"F17.wireOp",EDGE,"E34"),sQuery(id+"F17.wireOp",EDGE,"E35"),sQuery(id+"F17.wireOp",EDGE,"E36"),sQuery(id+"F17.wireOp",EDGE,"E37"),sQuery(id+"F17.wireOp",EDGE,"E38"),sQuery(id+"F17.wireOp",EDGE,"E39"),sQuery(id+"F17.wireOp",EDGE,"E40"),sQuery(id+"F17.wireOp",EDGE,"E41"),sQuery(id+"F17.wireOp",EDGE,"E42"),sQuery(id+"F17.wireOp",EDGE,"E43")])],"isStart":false});
            var sketch = newSketch(context, id + "F23", { "sketchPlane" : qUnion([Q0])});
            skLineSegment(sketch, "E80", {"start": v(-107.95, 139.45) * mm, "end": v(-116.84, 130.56) * mm});
            skLineSegment(sketch, "E81", {"start": v(-116.84, 130.56) * mm, "end": v(-73.66, 130.56) * mm});
            skLineSegment(sketch, "E82", {"start": v(-73.66, 130.56) * mm, "end": v(-82.55, 139.45) * mm});
            skLineSegment(sketch, "E83", {"start": v(-82.55, 139.45) * mm, "end": v(-107.95, 139.45) * mm});
            skSolve(sketch);
        }
        {
            var Q0;
            Q0 = qSketchRegion(id + "F23", true);
            extrude(context, id + "F24", {"entities" : qUnion([Q0]), "operationType" : NewBodyOperationType.REMOVE, "oppositeDirection" : true, "depth" : 0.38 * mm, "offsetDistance" : 25.4 * mm});
        }
        {
            var Q0;
            Q0=makeQuery(id+"F22.boolean.opBoolean","COPY",EDGE,{"derivedFrom":makeQuery(id+"F22.opExtrude","SWEPT_EDGE",EDGE,{"disambiguationData":[OSD([sQuery(id+"F21.wireOp",EDGE,"E58.right"),sQuery(id+"F21.wireOp",EDGE,"E64.trimOffspring")])]})});
            var Q1;
            Q1=makeQuery(id+"F22.boolean.opBoolean","COPY",EDGE,{"derivedFrom":makeQuery(id+"F22.opExtrude","SWEPT_EDGE",EDGE,{"disambiguationData":[OSD([sQuery(id+"F21.wireOp",EDGE,"E57.right"),sQuery(id+"F21.wireOp",EDGE,"E62")])]})});
            var Q2;
            Q2=makeQuery(id+"F22.boolean.opBoolean","COPY",EDGE,{"derivedFrom":makeQuery(id+"F22.opExtrude","SWEPT_EDGE",EDGE,{"disambiguationData":[OSD([sQuery(id+"F21.wireOp",EDGE,"E57.right"),sQuery(id+"F21.wireOp",EDGE,"E65.trimOffspring")])]})});
            var Q3;
            Q3=makeQuery(id+"F22.boolean.opBoolean","COPY",EDGE,{"derivedFrom":makeQuery(id+"F22.opExtrude","SWEPT_EDGE",EDGE,{"disambiguationData":[OSD([sQuery(id+"F21.wireOp",EDGE,"E58.right"),sQuery(id+"F21.wireOp",EDGE,"E66.trimOffspring")])]})});
            var Q4;
            Q4=makeQuery(id+"F22.boolean.opBoolean","COPY",EDGE,{"derivedFrom":makeQuery(id+"F22.opExtrude","SWEPT_EDGE",EDGE,{"disambiguationData":[OSD([sQuery(id+"F21.wireOp",EDGE,"E58.left"),sQuery(id+"F21.wireOp",EDGE,"E66.trimOffspring")])]})});
            var Q5;
            Q5=makeQuery(id+"F22.boolean.opBoolean","COPY",EDGE,{"derivedFrom":makeQuery(id+"F22.opExtrude","SWEPT_EDGE",EDGE,{"disambiguationData":[OSD([sQuery(id+"F21.wireOp",EDGE,"E57.left"),sQuery(id+"F21.wireOp",EDGE,"E65.trimOffspring")])]})});
            var Q6;
            Q6=makeQuery(id+"F22.boolean.opBoolean","COPY",EDGE,{"derivedFrom":makeQuery(id+"F22.opExtrude","SWEPT_EDGE",EDGE,{"disambiguationData":[OSD([sQuery(id+"F21.wireOp",EDGE,"E58.left"),sQuery(id+"F21.wireOp",EDGE,"E64.trimOffspring")])]})});
            var Q7;
            Q7=makeQuery(id+"F22.boolean.opBoolean","COPY",EDGE,{"derivedFrom":makeQuery(id+"F22.opExtrude","SWEPT_EDGE",EDGE,{"disambiguationData":[OSD([sQuery(id+"F21.wireOp",EDGE,"E57.left"),sQuery(id+"F21.wireOp",EDGE,"E62")])]})});
            var Q8;
            Q8=makeQuery(id+"F22.boolean.opBoolean","COPY",EDGE,{"derivedFrom":makeQuery(id+"F22.opExtrude","SWEPT_EDGE",EDGE,{"disambiguationData":[OSD([sQuery(id+"F21.wireOp",EDGE,"E70.top"),sQuery(id+"F21.wireOp",EDGE,"E70.left")])]})});
            var Q9;
            Q9=makeQuery(id+"F22.boolean.opBoolean","COPY",EDGE,{"derivedFrom":makeQuery(id+"F22.opExtrude","SWEPT_EDGE",EDGE,{"disambiguationData":[OSD([sQuery(id+"F21.wireOp",EDGE,"E68"),sQuery(id+"F21.wireOp",EDGE,"E69.trimOffspring")])]})});
            var Q10;
            Q10=makeQuery(id+"F22.boolean.opBoolean","COPY",EDGE,{"derivedFrom":makeQuery(id+"F22.opExtrude","SWEPT_EDGE",EDGE,{"disambiguationData":[OSD([sQuery(id+"F21.wireOp",EDGE,"E61.right"),sQuery(id+"F21.wireOp",EDGE,"E72")])]})});
            var Q11;
            Q11=makeQuery(id+"F22.boolean.opBoolean","COPY",EDGE,{"derivedFrom":makeQuery(id+"F22.opExtrude","SWEPT_EDGE",EDGE,{"disambiguationData":[OSD([sQuery(id+"F21.wireOp",EDGE,"E70.top"),sQuery(id+"F21.wireOp",EDGE,"E70.right")])]})});
            var Q12;
            Q12=makeQuery(id+"F22.boolean.opBoolean","COPY",EDGE,{"derivedFrom":makeQuery(id+"F22.opExtrude","SWEPT_EDGE",EDGE,{"disambiguationData":[OSD([sQuery(id+"F21.wireOp",EDGE,"E67"),sQuery(id+"F21.wireOp",EDGE,"E72")])]})});
            var Q13;
            Q13=makeQuery(id+"F22.boolean.opBoolean","COPY",EDGE,{"derivedFrom":makeQuery(id+"F22.opExtrude","SWEPT_EDGE",EDGE,{"disambiguationData":[OSD([sQuery(id+"F21.wireOp",EDGE,"E61.right"),sQuery(id+"F21.wireOp",EDGE,"E68")])]})});
            var Q14;
            Q14=makeQuery(id+"F22.boolean.opBoolean","COPY",EDGE,{"derivedFrom":makeQuery(id+"F22.opExtrude","SWEPT_EDGE",EDGE,{"disambiguationData":[OSD([sQuery(id+"F21.wireOp",EDGE,"E60.bottom"),sQuery(id+"F21.wireOp",EDGE,"E69.trimOffspring")])]})});
            var Q15;
            Q15=makeQuery(id+"F22.boolean.opBoolean","COPY",EDGE,{"derivedFrom":makeQuery(id+"F22.opExtrude","SWEPT_EDGE",EDGE,{"disambiguationData":[OSD([sQuery(id+"F21.wireOp",EDGE,"E63"),sQuery(id+"F21.wireOp",EDGE,"E70.left")])]})});
            var Q16;
            Q16=makeQuery(id+"F22.boolean.opBoolean","COPY",EDGE,{"derivedFrom":makeQuery(id+"F22.opExtrude","SWEPT_EDGE",EDGE,{"disambiguationData":[OSD([sQuery(id+"F21.wireOp",EDGE,"E59.right"),sQuery(id+"F21.wireOp",EDGE,"E71")])]})});
            var Q17;
            Q17=makeQuery(id+"F22.boolean.opBoolean","COPY",EDGE,{"derivedFrom":makeQuery(id+"F22.opExtrude","SWEPT_EDGE",EDGE,{"disambiguationData":[OSD([sQuery(id+"F21.wireOp",EDGE,"E70.right"),sQuery(id+"F21.wireOp",EDGE,"E71")])]})});
            var Q18;
            Q18=makeQuery(id+"F22.boolean.opBoolean","COPY",EDGE,{"derivedFrom":makeQuery(id+"F22.opExtrude","SWEPT_EDGE",EDGE,{"disambiguationData":[OSD([sQuery(id+"F21.wireOp",EDGE,"E59.right"),sQuery(id+"F21.wireOp",EDGE,"E63")])]})});
            var Q19;
            Q19=makeQuery(id+"F22.boolean.opBoolean","COPY",EDGE,{"derivedFrom":makeQuery(id+"F22.opExtrude","SWEPT_EDGE",EDGE,{"disambiguationData":[OSD([sQuery(id+"F21.wireOp",EDGE,"E60.bottom"),sQuery(id+"F21.wireOp",EDGE,"E67")])]})});
            var Q20;
            Q20=makeQuery(id+"F22.boolean.opBoolean","COPY",EDGE,{"derivedFrom":makeQuery(id+"F22.opExtrude","SWEPT_EDGE",EDGE,{"disambiguationData":[OSD([sQuery(id+"F21.wireOp",EDGE,"E73.top"),sQuery(id+"F21.wireOp",EDGE,"E73.left")])]})});
            var Q21;
            Q21=makeQuery(id+"F22.boolean.opBoolean","COPY",EDGE,{"derivedFrom":makeQuery(id+"F22.opExtrude","SWEPT_EDGE",EDGE,{"disambiguationData":[OSD([sQuery(id+"F21.wireOp",EDGE,"E74.top"),sQuery(id+"F21.wireOp",EDGE,"E74.left")])]})});
            var Q22;
            Q22=makeQuery(id+"F22.boolean.opBoolean","COPY",EDGE,{"derivedFrom":makeQuery(id+"F22.opExtrude","SWEPT_EDGE",EDGE,{"disambiguationData":[OSD([sQuery(id+"F21.wireOp",EDGE,"E73.bottom"),sQuery(id+"F21.wireOp",EDGE,"E73.left")])]})});
            var Q23;
            Q23=makeQuery(id+"F22.boolean.opBoolean","COPY",EDGE,{"derivedFrom":makeQuery(id+"F22.opExtrude","SWEPT_EDGE",EDGE,{"disambiguationData":[OSD([sQuery(id+"F21.wireOp",EDGE,"E74.bottom"),sQuery(id+"F21.wireOp",EDGE,"E74.left")])]})});
            var Q24;
            Q24=makeQuery(id+"F22.boolean.opBoolean","COPY",EDGE,{"derivedFrom":makeQuery(id+"F22.opExtrude","SWEPT_EDGE",EDGE,{"disambiguationData":[OSD([sQuery(id+"F21.wireOp",EDGE,"E73.bottom"),sQuery(id+"F21.wireOp",EDGE,"E73.right")])]})});
            var Q25;
            Q25=makeQuery(id+"F22.boolean.opBoolean","COPY",EDGE,{"derivedFrom":makeQuery(id+"F22.opExtrude","SWEPT_EDGE",EDGE,{"disambiguationData":[OSD([sQuery(id+"F21.wireOp",EDGE,"E74.bottom"),sQuery(id+"F21.wireOp",EDGE,"E74.right")])]})});
            var Q26;
            Q26=makeQuery(id+"F22.boolean.opBoolean","COPY",EDGE,{"derivedFrom":makeQuery(id+"F22.opExtrude","SWEPT_EDGE",EDGE,{"disambiguationData":[OSD([sQuery(id+"F21.wireOp",EDGE,"E73.top"),sQuery(id+"F21.wireOp",EDGE,"E73.right")])]})});
            var Q27;
            Q27=makeQuery(id+"F22.boolean.opBoolean","COPY",EDGE,{"derivedFrom":makeQuery(id+"F22.opExtrude","SWEPT_EDGE",EDGE,{"disambiguationData":[OSD([sQuery(id+"F21.wireOp",EDGE,"E74.top"),sQuery(id+"F21.wireOp",EDGE,"E74.right")])]})});
            var Q28;
            Q28=makeQuery(id+"F22.boolean.opBoolean","COPY",EDGE,{"derivedFrom":makeQuery(id+"F22.opExtrude","SWEPT_EDGE",EDGE,{"disambiguationData":[OSD([sQuery(id+"F21.wireOp",EDGE,"E75.top"),sQuery(id+"F21.wireOp",EDGE,"E75.right")])]})});
            var Q29;
            Q29=makeQuery(id+"F22.boolean.opBoolean","COPY",EDGE,{"derivedFrom":makeQuery(id+"F22.opExtrude","SWEPT_EDGE",EDGE,{"disambiguationData":[OSD([sQuery(id+"F21.wireOp",EDGE,"E75.top"),sQuery(id+"F21.wireOp",EDGE,"E75.left")])]})});
            var Q30;
            Q30=makeQuery(id+"F22.boolean.opBoolean","COPY",EDGE,{"derivedFrom":makeQuery(id+"F22.opExtrude","SWEPT_EDGE",EDGE,{"disambiguationData":[OSD([sQuery(id+"F21.wireOp",EDGE,"E75.bottom"),sQuery(id+"F21.wireOp",EDGE,"E75.right")])]})});
            var Q31;
            Q31=makeQuery(id+"F22.boolean.opBoolean","COPY",EDGE,{"derivedFrom":makeQuery(id+"F22.opExtrude","SWEPT_EDGE",EDGE,{"disambiguationData":[OSD([sQuery(id+"F21.wireOp",EDGE,"E75.bottom"),sQuery(id+"F21.wireOp",EDGE,"E75.left")])]})});
            var Q32;
            Q32=makeQuery(id+"F22.boolean.opBoolean","COPY",FACE,{"derivedFrom":makeQuery(id+"F22.opExtrude","CAP_FACE",FACE,{"disambiguationData":[OSD([sQuery(id+"F21.wireOp",EDGE,"E75.bottom"),sQuery(id+"F21.wireOp",EDGE,"E75.top"),sQuery(id+"F21.wireOp",EDGE,"E75.left"),sQuery(id+"F21.wireOp",EDGE,"E75.right")])],"isStart":false})});
            var Q33;
            Q33=makeQuery(id+"F22.boolean.opBoolean","COPY",FACE,{"derivedFrom":makeQuery(id+"F22.opExtrude","CAP_FACE",FACE,{"disambiguationData":[OSD([sQuery(id+"F21.wireOp",EDGE,"E74.bottom"),sQuery(id+"F21.wireOp",EDGE,"E74.top"),sQuery(id+"F21.wireOp",EDGE,"E74.left"),sQuery(id+"F21.wireOp",EDGE,"E74.right")])],"isStart":false})});
            var Q34;
            Q34=makeQuery(id+"F22.boolean.opBoolean","COPY",FACE,{"derivedFrom":makeQuery(id+"F22.opExtrude","CAP_FACE",FACE,{"disambiguationData":[OSD([sQuery(id+"F21.wireOp",EDGE,"E73.bottom"),sQuery(id+"F21.wireOp",EDGE,"E73.top"),sQuery(id+"F21.wireOp",EDGE,"E73.left"),sQuery(id+"F21.wireOp",EDGE,"E73.right")])],"isStart":false})});
            var Q35;
            Q35=makeQuery(id+"F22.boolean.opBoolean","COPY",FACE,{"derivedFrom":makeQuery(id+"F22.opExtrude","CAP_FACE",FACE,{"disambiguationData":[OSD([sQuery(id+"F21.wireOp",EDGE,"E60.bottom"),sQuery(id+"F21.wireOp",EDGE,"E61.right"),sQuery(id+"F21.wireOp",EDGE,"E67"),sQuery(id+"F21.wireOp",EDGE,"E68"),sQuery(id+"F21.wireOp",EDGE,"E69.trimOffspring"),sQuery(id+"F21.wireOp",EDGE,"E72")])],"isStart":false})});
            var Q36;
            Q36=makeQuery(id+"F22.boolean.opBoolean","COPY",FACE,{"derivedFrom":makeQuery(id+"F22.opExtrude","CAP_FACE",FACE,{"disambiguationData":[OSD([sQuery(id+"F21.wireOp",EDGE,"E59.right"),sQuery(id+"F21.wireOp",EDGE,"E63"),sQuery(id+"F21.wireOp",EDGE,"E70.top"),sQuery(id+"F21.wireOp",EDGE,"E70.left"),sQuery(id+"F21.wireOp",EDGE,"E70.right"),sQuery(id+"F21.wireOp",EDGE,"E71")])],"isStart":false})});
            var Q37;
            Q37=makeQuery(id+"F22.boolean.opBoolean","COPY",FACE,{"derivedFrom":makeQuery(id+"F22.opExtrude","CAP_FACE",FACE,{"disambiguationData":[OSD([sQuery(id+"F21.wireOp",EDGE,"E58.left"),sQuery(id+"F21.wireOp",EDGE,"E58.right"),sQuery(id+"F21.wireOp",EDGE,"E64.trimOffspring"),sQuery(id+"F21.wireOp",EDGE,"E66.trimOffspring")])],"isStart":false})});
            var Q38;
            Q38=makeQuery(id+"F22.boolean.opBoolean","COPY",FACE,{"derivedFrom":makeQuery(id+"F22.opExtrude","CAP_FACE",FACE,{"disambiguationData":[OSD([sQuery(id+"F21.wireOp",EDGE,"E57.left"),sQuery(id+"F21.wireOp",EDGE,"E57.right"),sQuery(id+"F21.wireOp",EDGE,"E62"),sQuery(id+"F21.wireOp",EDGE,"E65.trimOffspring")])],"isStart":false})});
            var Q39;
            Q39=makeQuery(id+"F18.opExtrude","SWEPT_EDGE",EDGE,{"disambiguationData":[OSD([sQuery(id+"F17.wireOp",EDGE,"E29.bottom"),sQuery(id+"F17.wireOp",EDGE,"E29.left")])]});
            var Q40;
            Q40=makeQuery(id+"F18.opExtrude","SWEPT_EDGE",EDGE,{"disambiguationData":[OSD([sQuery(id+"F17.wireOp",EDGE,"E29.left"),sQuery(id+"F17.wireOp",EDGE,"E31")])]});
            var Q41;
            Q41=makeQuery(id+"F18.opExtrude","SWEPT_EDGE",EDGE,{"disambiguationData":[OSD([sQuery(id+"F17.wireOp",EDGE,"E30.left"),sQuery(id+"F17.wireOp",EDGE,"E31")])]});
            var Q42;
            Q42=makeQuery(id+"F18.opExtrude","SWEPT_EDGE",EDGE,{"disambiguationData":[OSD([sQuery(id+"F17.wireOp",EDGE,"E30.top"),sQuery(id+"F17.wireOp",EDGE,"E30.left")])]});
            var Q43;
            Q43=makeQuery(id+"F18.opExtrude","SWEPT_EDGE",EDGE,{"disambiguationData":[OSD([sQuery(id+"F17.wireOp",EDGE,"E30.top"),sQuery(id+"F17.wireOp",EDGE,"E30.right")])]});
            var Q44;
            Q44=makeQuery(id+"F18.opExtrude","SWEPT_EDGE",EDGE,{"disambiguationData":[OSD([sQuery(id+"F17.wireOp",EDGE,"E30.bottom"),sQuery(id+"F17.wireOp",EDGE,"E30.right")])]});
            var Q45;
            Q45=makeQuery(id+"F18.opExtrude","SWEPT_EDGE",EDGE,{"disambiguationData":[OSD([sQuery(id+"F17.wireOp",EDGE,"E30.bottom"),sQuery(id+"F17.wireOp",EDGE,"E32.trimOffspring")])]});
            var Q46;
            Q46=makeQuery(id+"F18.opExtrude","SWEPT_EDGE",EDGE,{"disambiguationData":[OSD([sQuery(id+"F17.wireOp",EDGE,"E29.top"),sQuery(id+"F17.wireOp",EDGE,"E32.trimOffspring")])]});
            var Q47;
            Q47=makeQuery(id+"F18.opExtrude","SWEPT_EDGE",EDGE,{"disambiguationData":[OSD([sQuery(id+"F17.wireOp",EDGE,"E29.top"),sQuery(id+"F17.wireOp",EDGE,"E29.right")])]});
            var Q48;
            Q48=makeQuery(id+"F22.boolean.opBoolean","COPY",EDGE,{"derivedFrom":makeQuery(id+"F22.opExtrude","SWEPT_EDGE",EDGE,{"disambiguationData":[OSD([sQuery(id+"F21.wireOp",EDGE,"E76"),sQuery(id+"F21.wireOp",EDGE,"E78.trimOffspring")])]})});
            var Q49;
            Q49=makeQuery(id+"F22.boolean.opBoolean","COPY",EDGE,{"derivedFrom":makeQuery(id+"F22.opExtrude","SWEPT_EDGE",EDGE,{"disambiguationData":[OSD([sQuery(id+"F21.wireOp",EDGE,"E77"),sQuery(id+"F21.wireOp",EDGE,"E79.trimOffspring")])]})});
            var Q50;
            Q50=makeQuery(id+"F24.boolean.opBoolean","COPY",EDGE,{"derivedFrom":makeQuery(id+"F24.opExtrude","CAP_EDGE",EDGE,{"disambiguationData":[OSD([sQuery(id+"F23.wireOp",EDGE,"E83")])],"isStart":false})});
            var Q51;
            Q51=makeQuery(id+"F18.opExtrude","CAP_EDGE",EDGE,{"disambiguationData":[OSD([sQuery(id+"F17.wireOp",EDGE,"E29.left")])],"isStart":false});
            var Q52;
            Q52=makeQuery(id+"F18.opExtrude","CAP_EDGE",EDGE,{"disambiguationData":[OSD([sQuery(id+"F17.wireOp",EDGE,"E29.bottom")])],"isStart":false});
            var Q53;
            Q53=makeQuery(id+"F18.opExtrude","CAP_EDGE",EDGE,{"disambiguationData":[OSD([sQuery(id+"F17.wireOp",EDGE,"E31")])],"isStart":false});
            var Q54;
            Q54=makeQuery(id+"F18.opExtrude","CAP_EDGE",EDGE,{"disambiguationData":[OSD([sQuery(id+"F17.wireOp",EDGE,"E30.left")])],"isStart":false});
            var Q55;
            Q55=makeQuery(id+"F18.opExtrude","CAP_EDGE",EDGE,{"disambiguationData":[OSD([sQuery(id+"F17.wireOp",EDGE,"E32.trimOffspring")])],"isStart":false});
            var Q56;
            Q56=makeQuery(id+"F18.opExtrude","CAP_EDGE",EDGE,{"disambiguationData":[OSD([sQuery(id+"F17.wireOp",EDGE,"E29.right")])],"isStart":false});
            var Q57;
            Q57=makeQuery(id+"F18.opExtrude","SWEPT_EDGE",EDGE,{"disambiguationData":[OSD([sQuery(id+"F17.wireOp",EDGE,"E29.bottom"),sQuery(id+"F17.wireOp",EDGE,"E29.right")])]});
            var Q58;
            Q58=makeQuery(id+"F18.opExtrude","CAP_EDGE",EDGE,{"disambiguationData":[OSD([sQuery(id+"F17.wireOp",EDGE,"E47")])],"isStart":false});
            var Q59;
            Q59=makeQuery(id+"F18.opExtrude","SWEPT_EDGE",EDGE,{"disambiguationData":[OSD([sQuery(id+"F17.wireOp",EDGE,"E44"),sQuery(id+"F17.wireOp",EDGE,"E45")])]});
            var Q60;
            Q60=makeQuery(id+"F18.opExtrude","SWEPT_EDGE",EDGE,{"disambiguationData":[OSD([sQuery(id+"F17.wireOp",EDGE,"E45"),sQuery(id+"F17.wireOp",EDGE,"E46")])]});
            var Q61;
            Q61=makeQuery(id+"F18.opExtrude","SWEPT_EDGE",EDGE,{"disambiguationData":[OSD([sQuery(id+"F17.wireOp",EDGE,"E46"),sQuery(id+"F17.wireOp",EDGE,"E47")])]});
            var Q62;
            Q62=makeQuery(id+"F18.opExtrude","SWEPT_EDGE",EDGE,{"disambiguationData":[OSD([sQuery(id+"F17.wireOp",EDGE,"E47"),sQuery(id+"F17.wireOp",EDGE,"E48")])]});
            fillet(context, id + "F25", {"entities" : qUnion([Q0, Q1, Q2, Q3, Q4, Q5, Q6, Q7, Q8, Q9, Q10, Q11, Q12, Q13, Q14, Q15, Q16, Q17, Q18, Q19, Q20, Q21, Q22, Q23, Q24, Q25, Q26, Q27, Q28, Q29, Q30, Q31, Q32, Q33, Q34, Q35, Q36, Q37, Q38, Q39, Q40, Q41, Q42, Q43, Q44, Q45, Q46, Q47, Q48, Q49, Q50, Q51, Q52, Q53, Q54, Q55, Q56, Q57, Q58, Q59, Q60, Q61, Q62]), "radius" : 1.27 * mm, "tangentPropagation" : true, "allowEdgeOverflow" : false});
        }
        {
            var Q0;
            Q0=makeQuery(id+"F18.opExtrude","CAP_FACE",FACE,{"disambiguationData":[OSD([sQuery(id+"F17.wireOp",EDGE,"E29.bottom"),sQuery(id+"F17.wireOp",EDGE,"E29.top"),sQuery(id+"F17.wireOp",EDGE,"E29.left"),sQuery(id+"F17.wireOp",EDGE,"E29.right"),sQuery(id+"F17.wireOp",EDGE,"E30.bottom"),sQuery(id+"F17.wireOp",EDGE,"E30.top"),sQuery(id+"F17.wireOp",EDGE,"E30.left"),sQuery(id+"F17.wireOp",EDGE,"E30.right"),sQuery(id+"F17.wireOp",EDGE,"E31"),sQuery(id+"F17.wireOp",EDGE,"E32.trimOffspring"),sQuery(id+"F17.wireOp",EDGE,"E33"),sQuery(id+"F17.wireOp",EDGE,"E34"),sQuery(id+"F17.wireOp",EDGE,"E35"),sQuery(id+"F17.wireOp",EDGE,"E36"),sQuery(id+"F17.wireOp",EDGE,"E37"),sQuery(id+"F17.wireOp",EDGE,"E38"),sQuery(id+"F17.wireOp",EDGE,"E39"),sQuery(id+"F17.wireOp",EDGE,"E40"),sQuery(id+"F17.wireOp",EDGE,"E41"),sQuery(id+"F17.wireOp",EDGE,"E42"),sQuery(id+"F17.wireOp",EDGE,"E43")])],"isStart":false});
            var sketch = newSketch(context, id + "F26", { "sketchPlane" : qUnion([Q0])});
            skCircle(sketch, "E84", {"center": v(-104.14, 134.37) * mm, "radius": 1.52 * mm});
            skCircle(sketch, "E85", {"center": v(-86.36, 134.37) * mm, "radius": 1.52 * mm});
            skSolve(sketch);
        }
        {
            var Q0;
            Q0 = qSketchRegion(id + "F26", true);
            extrude(context, id + "F27", {"entities" : qUnion([Q0]), "operationType" : NewBodyOperationType.REMOVE, "endBound" : BoundingType.THROUGH_ALL, "oppositeDirection" : true, "depth" : 25.4 * mm, "offsetDistance" : 25.4 * mm});
        }
    });
